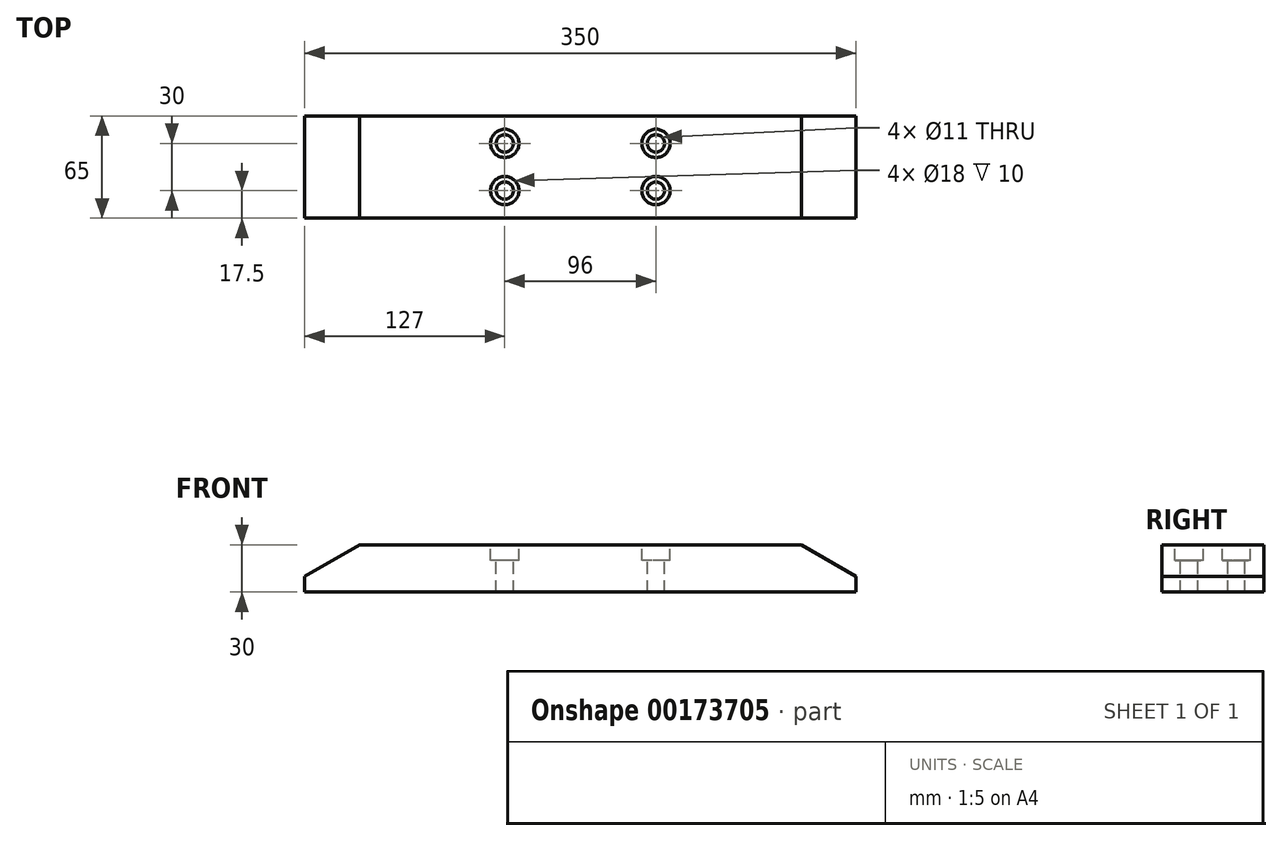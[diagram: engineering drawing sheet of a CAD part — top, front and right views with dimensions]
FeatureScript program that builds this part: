
annotation { "Feature Type Name" : "Feature", "Feature Type Description" : "" }
export const myFeature = defineFeature(function(context is Context, id is Id, definition is map)
    precondition{}
    {
        {
            var Q0;
            Q0=qCreatedBy(makeId("Top.planeOp"),FACE);
            var sketch = newSketch(context, id + "F0", { "sketchPlane" : qUnion([Q0])});
            skLineSegment(sketch, "E0.bottom", {"start": v(-175, -32.5) * mm, "end": v(175, -32.5) * mm});
            skLineSegment(sketch, "E0.top", {"start": v(-175, 32.5) * mm, "end": v(175, 32.5) * mm});
            skLineSegment(sketch, "E0.left", {"start": v(-175, -32.5) * mm, "end": v(-175, 32.5) * mm});
            skLineSegment(sketch, "E0.right", {"start": v(175, -32.5) * mm, "end": v(175, 32.5) * mm});
            skPoint(sketch, "E0.middle", {"position": v(0, 0) * mm});
            skSolve(sketch);
        }
        {
            var Q0;
            Q0=qSketchRegion(id+"F0",true);
            extrude(context, id + "F1", {"entities" : qUnion([Q0]), "depth" : 30 * mm});
        }
        {
            var Q0;
            Q0=makeQuery(id+"F1.opExtrude","CAP_FACE",FACE,{"disambiguationData":[OSD([sQuery(id+"F0.wireOp",EDGE,"E0.bottom"),sQuery(id+"F0.wireOp",EDGE,"E0.top"),sQuery(id+"F0.wireOp",EDGE,"E0.left"),sQuery(id+"F0.wireOp",EDGE,"E0.right")])],"isStart":false});
            var sketch = newSketch(context, id + "F2", { "sketchPlane" : qUnion([Q0])});
            skLineSegment(sketch, "E1", {"start": v(0, 29.46) * mm, "end": v(0, 0) * mm, "construction": true});
            skLineSegment(sketch, "E2", {"start": v(0, 0) * mm, "end": v(139.84, 0) * mm, "construction": true});
            skPoint(sketch, "E3", {"position": v(-48, 15) * mm});
            skPoint(sketch, "E4.MirrorP", {"position": v(48, 15) * mm});
            skPoint(sketch, "E5.MirrorP", {"position": v(48, -15) * mm});
            skPoint(sketch, "E6.MirrorP", {"position": v(-48, -15) * mm});
            skSolve(sketch);
        }
        {
            var Q0;
            Q0=sQuery(id+"F2.wireOp",VERTEX,"E3");
            var Q1;
            Q1=sQuery(id+"F2.wireOp",VERTEX,"E4.MirrorP");
            var Q2;
            Q2=sQuery(id+"F2.wireOp",VERTEX,"E5.MirrorP");
            var Q3;
            Q3=sQuery(id+"F2.wireOp",VERTEX,"E6.MirrorP");
            var Q4;
            Q4=makeQuery(id+"F1.opExtrude","SWEPT_BODY",BODY,{"disambiguationData":[OSD([sQuery(id+"F0.wireOp",EDGE,"E0.bottom"),sQuery(id+"F0.wireOp",EDGE,"E0.top"),sQuery(id+"F0.wireOp",EDGE,"E0.left"),sQuery(id+"F0.wireOp",EDGE,"E0.right")])]});
            hole(context, id + "F3", {"style" : HoleStyle.C_BORE, "endStyle" : HoleEndStyle.THROUGH, "holeDiameter" : 11 * mm, "cBoreDiameter" : 18 * mm, "cBoreDepth" : 10 * mm, "startFromSketch" : true, "locations" : qUnion([Q0, Q1, Q2, Q3]), "scope" : qUnion([Q4]), "isTappedThrough" : true});
        }
        {
            var Q0;
            Q0=makeQuery(id+"F1.opExtrude","CAP_EDGE",EDGE,{"disambiguationData":[OSD([sQuery(id+"F0.wireOp",EDGE,"E0.left")])],"isStart":false});
            var Q1;
            Q1=makeQuery(id+"F1.opExtrude","CAP_EDGE",EDGE,{"disambiguationData":[OSD([sQuery(id+"F0.wireOp",EDGE,"E0.right")])],"isStart":false});
            chamfer(context, id + "F4", {"entities" : qUnion([Q0, Q1]), "chamferType" : ChamferType.OFFSET_ANGLE, "width" : 20 * mm, "oppositeDirection" : false, "angle" : 60 * degree, "tangentPropagation" : true});
        }
    });
